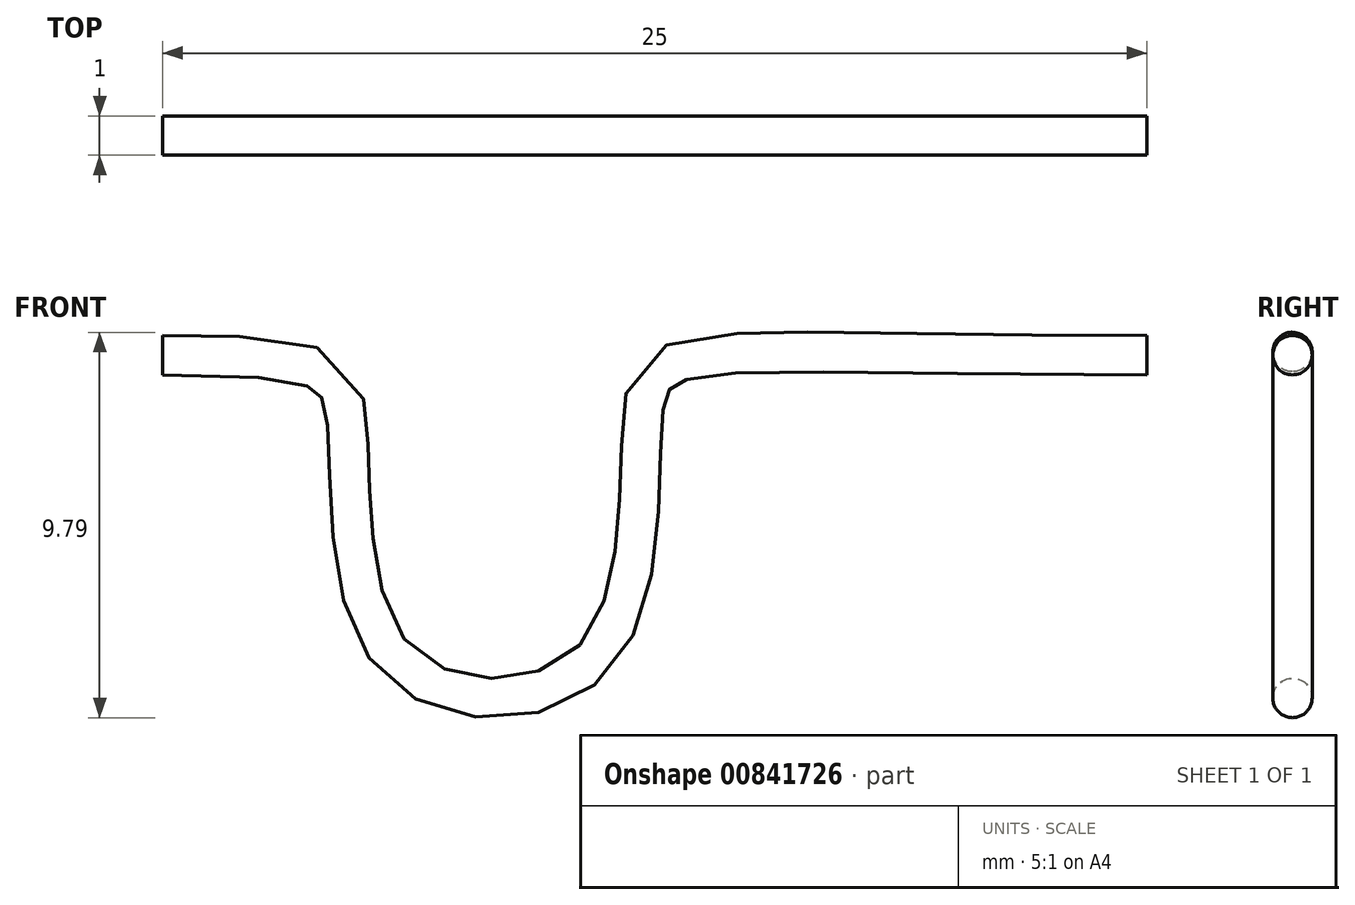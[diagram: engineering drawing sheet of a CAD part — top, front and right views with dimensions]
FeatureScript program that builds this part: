
annotation { "Feature Type Name" : "Feature", "Feature Type Description" : "" }
export const myFeature = defineFeature(function(context is Context, id is Id, definition is map)
    precondition{}
    {
        {
            var Q0;
            Q0=qCreatedBy(makeId("Front.planeOp"),FACE);
            var sketch = newSketch(context, id + "F0", { "sketchPlane" : qUnion([Q0])});
            skFitSpline(sketch, "E0", {"points": [v(-25, 0) * mm, v(-20.32, -1.68) * mm, v(-19.07, -7.74) * mm, v(-14.07, -7.74) * mm, v(-12.82, -1.68) * mm, v(0, 0) * mm], "startDerivative": vector(71.77, 0) * mm, "endDerivative": vector(128.01, 0) * mm});
            skSolve(sketch);
        }
        {
            var Q0;
            Q0=qCreatedBy(makeId("Right.planeOp"),FACE);
            var sketch = newSketch(context, id + "F1", { "sketchPlane" : qUnion([Q0])});
            skCircle(sketch, "E1", {"center": v(0, 0) * mm, "radius": 0.5 * mm});
            skSolve(sketch);
        }
        {
            var Q0;
            Q0 = qSketchRegion(id + "F1", true);
            var Q1;
            Q1 = qConstructionFilter(qBodyType(qCreatedBy(id + "F0" ,EDGE), BodyType.WIRE), ConstructionObject.NO);
            sweep(context, id + "F2", {"profiles" : qUnion([Q0]), "path" : qUnion([Q1])});
        }
    });
